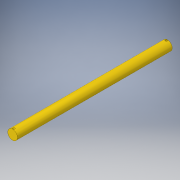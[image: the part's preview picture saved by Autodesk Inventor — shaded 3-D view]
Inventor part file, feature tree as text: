
AUTODESK INVENTOR PART (.ipt)
format: ipt  version: 2016 (Build 200138000, 138)  size: 105,984 bytes
history: native  units: in
note: dims shown in document units (in); Inventor stores cm internally (conversion verified against a paired STEP export)
features: sketch x3, extrude x2
ambient origin geometry x8: Origin, YZ Plane, XZ Plane, XY Plane, X Axis, Y Axis, Z Axis, Center Point
bodies: Solid1 (feature_tree)
feature tree (5):
  extrude  "Extrusion1"  Depth=8.0in TaperAngle=0.0deg
  extrude  "Extrusion4"  Depth=0.06in
  sketch  "Sketch5"  dims[d16=0.1in d17=0.6in d18=0.0in d19=0.1in]
  sketch  "Sketch1"  dims[d0=0.5in d1=8.0in d2=0.0in]
  sketch  "Sketch4"  dims[d13=0.06in d15=0.06in]
